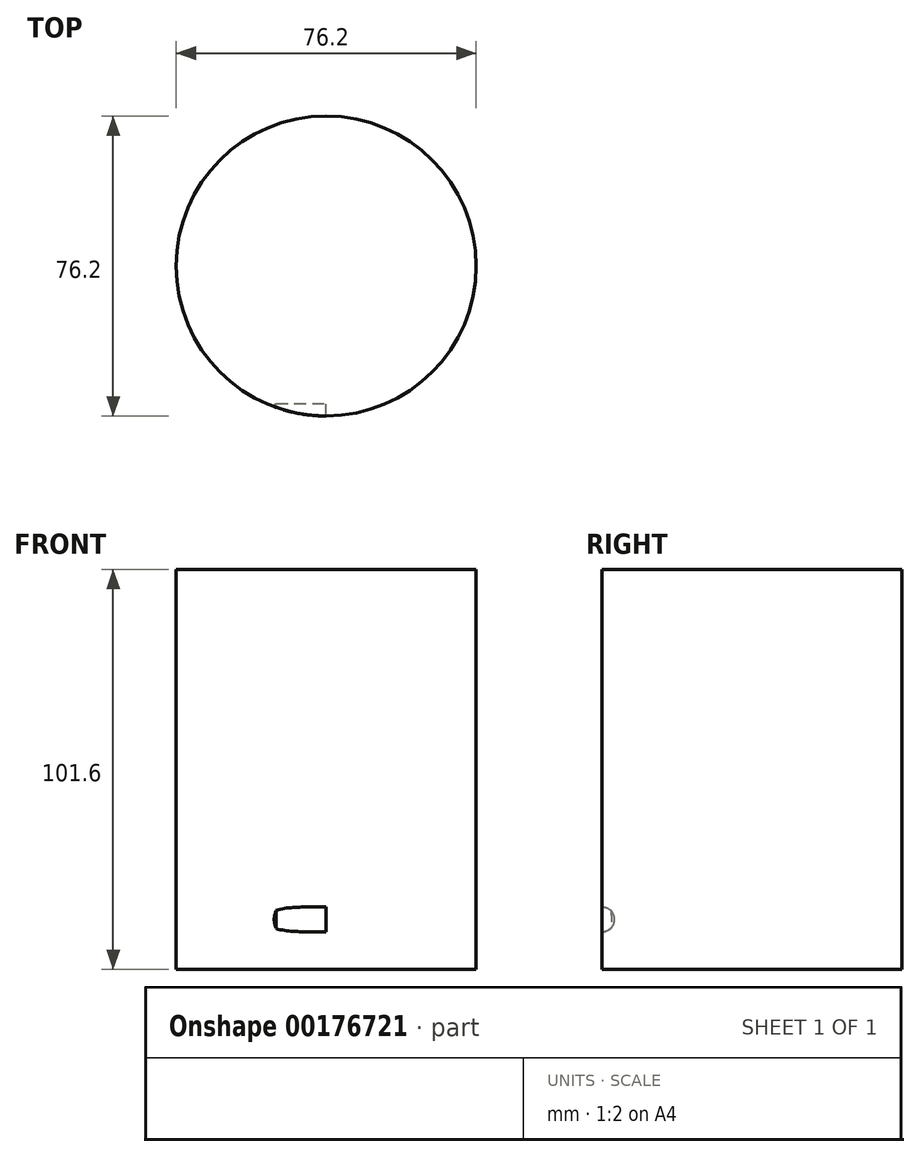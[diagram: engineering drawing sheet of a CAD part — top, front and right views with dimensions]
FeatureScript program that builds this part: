
annotation { "Feature Type Name" : "Feature", "Feature Type Description" : "" }
export const myFeature = defineFeature(function(context is Context, id is Id, definition is map)
    precondition{}
    {
        {
            var Q0;
            Q0=qCreatedBy(makeId("Top.planeOp"),FACE);
            var sketch = newSketch(context, id + "F0", { "sketchPlane" : qUnion([Q0])});
            skCircle(sketch, "E0", {"center": v(0, 0) * mm, "radius": 38.1 * mm});
            skSolve(sketch);
        }
        {
            var Q0;
            Q0 = qSketchRegion(id + "F0", true);
            extrude(context, id + "F1", {"entities" : qUnion([Q0]), "depth" : 101.6 * mm});
        }
        {
            var Q0;
            Q0=qCreatedBy(makeId("Right.planeOp"),FACE);
            var sketch = newSketch(context, id + "F2", { "sketchPlane" : qUnion([Q0])});
            skPoint(sketch, "E1", {"position": v(-38.1, 12.7) * mm});
            skLineSegment(sketch, "E2", {"start": v(-38.1, 0) * mm, "end": v(-38.1, 101.6) * mm, "construction": true});
            skSolve(sketch);
        }
        {
            var Q0;
            Q0=sQuery(id+"F2.wireOp",VERTEX,"E1");
            var Q1;
            Q1=makeQuery(id+"F1.opExtrude","SWEPT_BODY",BODY,{"disambiguationData":[OSD([sQuery(id+"F0.wireOp",EDGE,"E0")])]});
            hole(context, id + "F3", {"style" : HoleStyle.SIMPLE, "endStyle" : HoleEndStyle.BLIND, "holeDiameter" : 6.35 * mm, "holeDepth" : 12.7 * mm, "locations" : qUnion([Q0]), "scope" : qUnion([Q1])});
        }
    });
